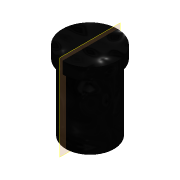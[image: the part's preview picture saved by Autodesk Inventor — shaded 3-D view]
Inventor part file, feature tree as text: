
AUTODESK INVENTOR PART (.ipt)
format: ipt  version: 2022 (Build 260153000, 153)  size: 96,256 bytes
history: native  units: in
note: dims shown in document units (in); Inventor stores cm internally (conversion verified against a paired STEP export)
features: extrude x2, sketch x2, plane x1
ambient origin geometry x8: Origin, YZ Plane, XZ Plane, XY Plane, X Axis, Y Axis, Z Axis, Center Point
bodies: Solid1 (feature_tree)
feature tree (5):
  extrude  "Extrusion1"  Depth=0.7835in TaperAngle=0.0deg
  extrude  "Extrusion2"  Depth=0.1181in TaperAngle=0.0deg
  plane  "Arbeitsebene1"
  sketch  "Sketch1"  dims[d0=0.4803in d1=0.7835in d2=0.0in]
  sketch  "Sketch2"  dims[d3=0.5512in d4=0.1181in d5=0.0in d6=0.0in]
